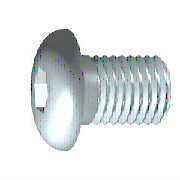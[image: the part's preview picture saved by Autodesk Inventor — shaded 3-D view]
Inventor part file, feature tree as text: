
AUTODESK INVENTOR PART (.ipt)
format: ipt  version: 2021 (Build 250183000, 183)  size: 202,240 bytes
history: native  units: mm (DEFAULTED — no unit token found)
features: sketch x3, extrude x2, other x1, plane x1, chamfer x1
ambient origin geometry x7: Origin, YZ Plane, XY Plane, X Axis, Y Axis, Z Axis, Center Point
bodies: Solid1 (feature_tree)
feature tree (8):
  other  "Körper"
  extrude  "Loch"  Depth=0.49076mm
  plane  "Work Plane1"
  extrude  "Extrusion3"  Depth=2.75mm
  chamfer  "Fase3"  Distance=5.0mm
  sketch  "Skizze1"  dims[d0=23.4mm d1=0.49076mm]
  sketch  "Skizze2"  dims[d2=2.75mm d3=1.56mm]
  sketch  "Skizze4"  dims[d4=60.0deg d5=5.0mm d6=5.0mm d7=3.464102mm d8=9.5mm d10=90.0deg d11=10.0mm d9=0.0mm d12=23.4mm d13=0.0mm d14=0.49076mm d15=0.49076mm d16=2.375mm d17=0.0mm d18=0.0mm d19=25.0mm d27=45.0deg d28=0.2mm d29=0.2mm d30=3.0mm d31=0.0mm d32=0.5mm d33=2.0mm d34=45.0deg]
